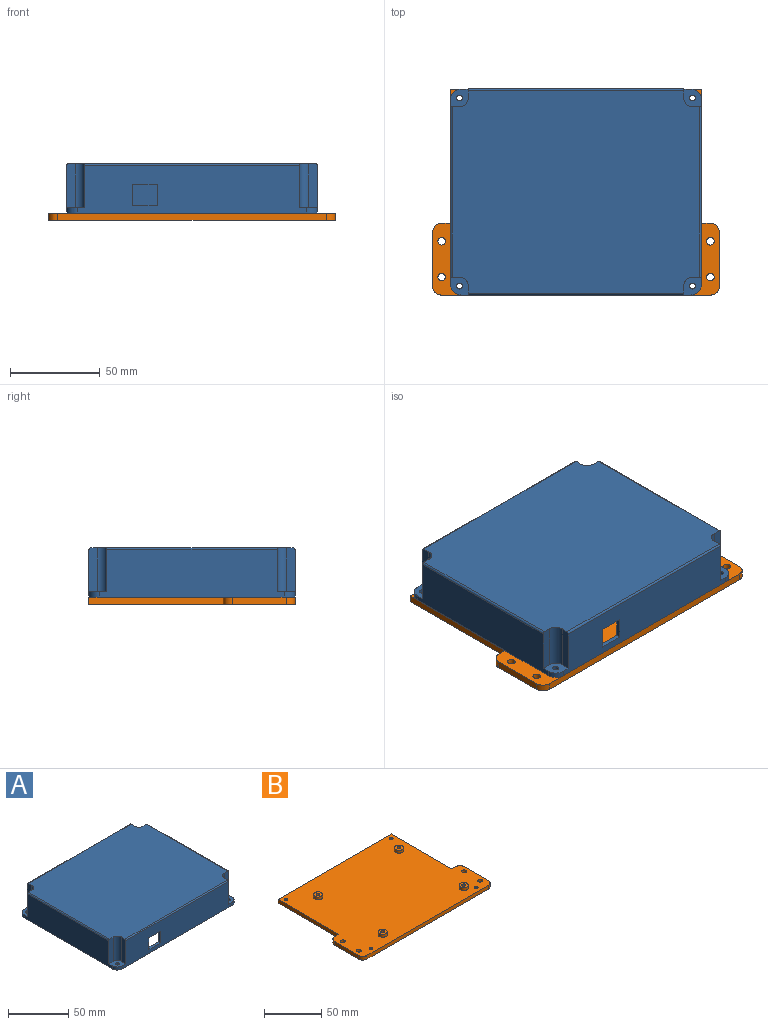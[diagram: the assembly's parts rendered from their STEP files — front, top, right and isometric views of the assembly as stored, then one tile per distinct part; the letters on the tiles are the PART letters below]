
ASSEMBLY  parts=2 mates=1
PART A: 55 faces, bbox 140x115x27.5 mm
  f0: plane 128x26.5mm, normal (0,-1,0), area 3048.3mm2, adj f6,f14,f15,f16,f39,f41,f43,f46
  f1: plane 116x25mm, normal (0,1,0), area 2738mm2, adj f10,f14,f20,f24,f51,f52,f53,f54
  f2: plane 103x26.5mm, normal (-1,0,0), area 2541.5mm2, adj f7,f14,f15,f18,f35,f37,f43,f44
  f3: plane 102.98x26.5mm, normal (1,0,0), area 2541.4mm2, adj f8,f14,f16,f17,f31,f32,f39,f40
  f4: plane 128x26.5mm, normal (0,1,0), area 3210.3mm2, adj f9,f14,f17,f18,f31,f34,f35,f38
  f5: plane 138x113mm, normal (0,0,1), area 15292.3mm2, adj f6,f7,f8,f9,f32,f33,f34,f36
  f6: cylinder r=1mm len=120.27mm, axis (-1,0,0), area 188.9mm2, adj f0,f5,f41,f46
  f7: cylinder r=1mm len=95mm, axis (0,1,0), area 149.2mm2, adj f2,f5,f37,f44
  f8: cylinder r=1mm len=95mm, axis (0,-1,0), area 149.2mm2, adj f3,f5,f32,f40
  f9: cylinder r=1mm len=120.27mm, axis (1,0,0), area 188.9mm2, adj f4,f5,f34,f38
  f10: plane 135x110mm, normal (0,0,-1), area 14519.9mm2, adj f1,f11,f12,f13,f19,f20,f21,f22
  f11: plane 116x25mm, normal (0,-1,0), area 2900mm2, adj f10,f14,f25,f29
  f12: plane 91x25mm, normal (-1,0,0), area 2275mm2, adj f10,f14,f23,f26
  f13: plane 91x25mm, normal (1,0,0), area 2275mm2, adj f10,f14,f19,f28
  f14: plane 140x115mm, normal (0,0,-1), area 1515mm2, adj f0,f1,f2,f3,f4,f11,f12,f13
  f15: cylinder r=6mm len=6mm, axis (0,0,-1), area 28.3mm2, adj f0,f2,f14,f43
  f16: cylinder r=6mm len=6.02mm, axis (0,0,-1), area 28.3mm2, adj f0,f3,f14,f39
  f17: cylinder r=6mm len=6.02mm, axis (0,0,-1), area 28.3mm2, adj f3,f4,f14,f31
  f18: cylinder r=6mm len=6mm, axis (0,0,-1), area 28.3mm2, adj f2,f4,f14,f35
  f19: plane 25x3.5mm, normal (0,1,0), area 87.5mm2, adj f10,f13,f14,f21
  f20: plane 25x3.5mm, normal (1,0,0), area 87.5mm2, adj f1,f10,f14,f21
  f21: cylinder r=6mm len=25mm, axis (0,0,1), area 235.6mm2, adj f10,f14,f19,f20
  f22: cylinder r=6mm len=25mm, axis (0,0,1), area 236.3mm2, adj f10,f14,f23,f24
  f23: plane 25x3.47mm, normal (0,1,0), area 86.8mm2, adj f10,f12,f14,f22
  f24: plane 25x3.5mm, normal (-1,0,0), area 87.5mm2, adj f1,f10,f14,f22
  f25: plane 25x3.5mm, normal (-1,0,0), area 87.5mm2, adj f10,f11,f14,f27
  f26: plane 25x3.47mm, normal (0,-1,0), area 86.8mm2, adj f10,f12,f14,f27
  f27: cylinder r=6mm len=25mm, axis (0,0,1), area 236.3mm2, adj f10,f14,f25,f26
  f28: plane 25x3.5mm, normal (0,-1,0), area 87.5mm2, adj f10,f13,f14,f30
  f29: plane 25x3.5mm, normal (1,0,0), area 87.5mm2, adj f10,f11,f14,f30
  f30: cylinder r=6mm len=25mm, axis (0,0,1), area 235.6mm2, adj f10,f14,f28,f29
  f31: plane 10x10mm, normal (0,0,1), area 78mm2, adj f3,f4,f17,f32,f33,f34,f50
  f32: plane 24.5x5mm, normal (0,1,0), area 122.3mm2, adj f3,f5,f8,f31,f33
  f33: cylinder r=5mm len=24.5mm, axis (0,0,-1), area 195.7mm2, adj f5,f31,f32,f34
  f34: plane 24.51x4.88mm, normal (1,-0.03,0), area 119mm2, adj f4,f5,f9,f31,f33
  f35: plane 10x10mm, normal (0,0,1), area 78mm2, adj f2,f4,f18,f36,f37,f38,f49
  f36: cylinder r=5mm len=24.5mm, axis (0,0,-1), area 195.7mm2, adj f5,f35,f37,f38
  f37: plane 24.5x5mm, normal (0,1,0), area 122.3mm2, adj f2,f5,f7,f35,f36
  f38: plane 24.51x4.88mm, normal (-1,-0.03,0), area 119mm2, adj f4,f5,f9,f35,f36
  f39: plane 10x10mm, normal (0,0,1), area 78mm2, adj f0,f3,f16,f40,f41,f42,f48
  f40: plane 24.5x5mm, normal (0,-1,0), area 122.3mm2, adj f3,f5,f8,f39,f42
  f41: plane 24.51x4.88mm, normal (1,0.03,0), area 119mm2, adj f0,f5,f6,f39,f42
  f42: cylinder r=5mm len=24.5mm, axis (0,0,-1), area 195.7mm2, adj f5,f39,f40,f41
  f43: plane 10x10mm, normal (0,0,1), area 78mm2, adj f0,f2,f15,f44,f45,f46,f47
  f44: plane 24.5x5mm, normal (0,-1,0), area 122.3mm2, adj f2,f5,f7,f43,f45
  f45: cylinder r=5mm len=24.5mm, axis (0,0,-1), area 195.7mm2, adj f5,f43,f44,f46
  f46: plane 24.51x4.88mm, normal (-1,0.03,0), area 119mm2, adj f0,f5,f6,f43,f45
  f47: cylinder r=1.65mm len=3.3mm, axis (0,0,-1), area 31.1mm2, adj f14,f43
  f48: cylinder r=1.65mm len=3.3mm, axis (0,0,-1), area 31.1mm2, adj f14,f39
  f49: cylinder r=1.65mm len=3.3mm, axis (0,0,-1), area 31.1mm2, adj f14,f35
  f50: cylinder r=1.65mm len=3.3mm, axis (0,0,-1), area 31.1mm2, adj f14,f31
  f51: plane 13.5x2.5mm, normal (0,0,-1), area 33.7mm2, adj f0,f1,f52,f54
  f52: plane 12x2.5mm, normal (1,0,0), area 30mm2, adj f0,f1,f51,f53
  f53: plane 13.5x2.5mm, normal (0,0,1), area 33.7mm2, adj f0,f1,f52,f54
  f54: plane 12x2.5mm, normal (-1,0,0), area 30mm2, adj f0,f1,f51,f53
PART B: 90 faces, bbox 160x115x7 mm
  f0: cylinder r=1.7mm len=4.5mm, axis (0,0,-1), area 48.1mm2, adj f9,f89
  f1: cylinder r=1.7mm len=4.5mm, axis (0,0,-1), area 48.1mm2, adj f12,f82
  f2: cylinder r=1.7mm len=4.5mm, axis (0,0,-1), area 48.1mm2, adj f14,f75
  f3: cylinder r=1.7mm len=4.5mm, axis (0,0,-1), area 48.1mm2, adj f16,f68
  f4: cylinder r=1.6mm len=3.2mm, axis (0,0,-1), area 15.1mm2, adj f33,f61
  f5: cylinder r=1.6mm len=3.2mm, axis (0,0,-1), area 15.1mm2, adj f33,f54
  f6: cylinder r=1.6mm len=3.2mm, axis (0,0,-1), area 15.1mm2, adj f33,f47
  f7: cylinder r=1.6mm len=3.2mm, axis (0,0,-1), area 15.1mm2, adj f33,f40
  f8: cylinder r=4mm len=8mm, axis (0,0,-1), area 75.4mm2, adj f9,f33
  f9: plane 8x8mm, normal (0,0,1), area 41.2mm2, adj f0,f8
  f10: plane 160x115mm, normal (0,0,-1), area 16613.5mm2, adj f17,f18,f19,f20,f21,f22,f23,f24
  f11: cylinder r=4mm len=8mm, axis (0,0,-1), area 75.4mm2, adj f12,f33
  f12: plane 8x8mm, normal (0,0,1), area 41.2mm2, adj f1,f11
  f13: cylinder r=4mm len=8mm, axis (0,0,-1), area 75.4mm2, adj f14,f33
  f14: plane 8x8mm, normal (0,0,1), area 41.2mm2, adj f2,f13
  f15: cylinder r=4mm len=8mm, axis (0,0,-1), area 75.4mm2, adj f16,f33
  f16: plane 8x8mm, normal (0,0,1), area 41.2mm2, adj f3,f15
  f17: plane 75x4mm, normal (-1,0,0), area 300mm2, adj f10,f18,f32,f33
  f18: plane 5x4mm, normal (0,1,0), area 20mm2, adj f10,f17,f19,f33
  f19: cylinder r=5mm len=5mm, axis (0,0,-1), area 31.4mm2, adj f10,f18,f20,f33
  f20: plane 30x4mm, normal (-1,0,0), area 120mm2, adj f10,f19,f21,f33
  f21: cylinder r=5mm len=5mm, axis (0,0,-1), area 31.4mm2, adj f10,f20,f22,f33
  f22: plane 150x4mm, normal (0,-1,0), area 600mm2, adj f10,f21,f23,f33
  f23: cylinder r=5mm len=5mm, axis (0,0,-1), area 31.4mm2, adj f10,f22,f24,f33
  f24: plane 30x4mm, normal (1,0,0), area 120mm2, adj f10,f23,f25,f33
  f25: cylinder r=5mm len=5mm, axis (0,0,-1), area 31.4mm2, adj f10,f24,f26,f33
  f26: plane 5x4mm, normal (0,1,0), area 20mm2, adj f10,f25,f27,f33
  f27: plane 75x4mm, normal (1,0,0), area 300mm2, adj f10,f26,f32,f33
  f28: cylinder r=2.1mm len=4.2mm, axis (0,0,-1), area 52.8mm2, adj f10,f33
  f29: cylinder r=2.1mm len=4.2mm, axis (0,0,-1), area 52.8mm2, adj f10,f33
  f30: cylinder r=2.1mm len=4.2mm, axis (0,0,-1), area 52.8mm2, adj f10,f33
  f31: cylinder r=2.1mm len=4.2mm, axis (0,0,-1), area 52.8mm2, adj f10,f33
  f32: plane 140x4mm, normal (0,1,0), area 560mm2, adj f10,f17,f27,f33
  f33: plane 160x115mm, normal (0,0,1), area 16589.9mm2, adj f4,f5,f6,f7,f8,f11,f13,f15
  f34: plane 3.18x2.5mm, normal (0,1,0), area 7.9mm2, adj f10,f35,f39,f40
  f35: plane 2.75x2.5mm, normal (0.87,0.5,0), area 7.9mm2, adj f10,f34,f36,f40
  f36: plane 2.75x2.5mm, normal (0.87,-0.5,0), area 7.9mm2, adj f10,f35,f37,f40
  f37: plane 3.18x2.5mm, normal (0,-1,0), area 7.9mm2, adj f10,f36,f38,f40
  f38: plane 2.75x2.5mm, normal (-0.87,-0.5,0), area 7.9mm2, adj f10,f37,f39,f40
  f39: plane 2.75x2.5mm, normal (-0.87,0.5,0), area 7.9mm2, adj f10,f34,f38,f40
  f40: plane 6.35x5.5mm, normal (0,0,-1), area 18.2mm2, adj f7,f34,f35,f36,f37,f38,f39
  f41: plane 3.18x2.5mm, normal (0,1,0), area 7.9mm2, adj f10,f42,f46,f47
  f42: plane 2.75x2.5mm, normal (0.87,0.5,0), area 7.9mm2, adj f10,f41,f43,f47
  f43: plane 2.75x2.5mm, normal (0.87,-0.5,0), area 7.9mm2, adj f10,f42,f44,f47
  f44: plane 3.18x2.5mm, normal (0,-1,0), area 7.9mm2, adj f10,f43,f45,f47
  f45: plane 2.75x2.5mm, normal (-0.87,-0.5,0), area 7.9mm2, adj f10,f44,f46,f47
  f46: plane 2.75x2.5mm, normal (-0.87,0.5,0), area 7.9mm2, adj f10,f41,f45,f47
  f47: plane 6.35x5.5mm, normal (0,0,-1), area 18.2mm2, adj f6,f41,f42,f43,f44,f45,f46
  f48: plane 2.75x2.5mm, normal (-0.87,0.5,0), area 7.9mm2, adj f10,f49,f53,f54
  f49: plane 3.18x2.5mm, normal (0,1,0), area 7.9mm2, adj f10,f48,f50,f54
  f50: plane 2.75x2.5mm, normal (0.87,0.5,0), area 7.9mm2, adj f10,f49,f51,f54
  f51: plane 2.75x2.5mm, normal (0.87,-0.5,0), area 7.9mm2, adj f10,f50,f52,f54
  f52: plane 3.18x2.5mm, normal (0,-1,0), area 7.9mm2, adj f10,f51,f53,f54
  f53: plane 2.75x2.5mm, normal (-0.87,-0.5,0), area 7.9mm2, adj f10,f48,f52,f54
  f54: plane 6.35x5.5mm, normal (0,0,-1), area 18.2mm2, adj f5,f48,f49,f50,f51,f52,f53
  f55: plane 3.18x2.5mm, normal (0,1,0), area 7.9mm2, adj f10,f56,f60,f61
  f56: plane 2.75x2.5mm, normal (0.87,0.5,0), area 7.9mm2, adj f10,f55,f57,f61
  f57: plane 2.75x2.5mm, normal (0.87,-0.5,0), area 7.9mm2, adj f10,f56,f58,f61
  f58: plane 3.18x2.5mm, normal (0,-1,0), area 7.9mm2, adj f10,f57,f59,f61
  f59: plane 2.75x2.5mm, normal (-0.87,-0.5,0), area 7.9mm2, adj f10,f58,f60,f61
  f60: plane 2.75x2.5mm, normal (-0.87,0.5,0), area 7.9mm2, adj f10,f55,f59,f61
  f61: plane 6.35x5.5mm, normal (0,0,-1), area 18.2mm2, adj f4,f55,f56,f57,f58,f59,f60
  f62: plane 3.18x2.5mm, normal (0,1,0), area 7.9mm2, adj f10,f63,f67,f68
  f63: plane 2.75x2.5mm, normal (0.87,0.5,0), area 7.9mm2, adj f10,f62,f64,f68
  f64: plane 2.75x2.5mm, normal (0.87,-0.5,0), area 7.9mm2, adj f10,f63,f65,f68
  f65: plane 3.18x2.5mm, normal (0,-1,0), area 7.9mm2, adj f10,f64,f66,f68
  f66: plane 2.75x2.5mm, normal (-0.87,-0.5,0), area 7.9mm2, adj f10,f65,f67,f68
  f67: plane 2.75x2.5mm, normal (-0.87,0.5,0), area 7.9mm2, adj f10,f62,f66,f68
  f68: plane 6.35x5.5mm, normal (0,0,-1), area 17.1mm2, adj f3,f62,f63,f64,f65,f66,f67
  f69: plane 2.75x2.5mm, normal (0.87,-0.5,0), area 7.9mm2, adj f10,f70,f74,f75
  f70: plane 3.18x2.5mm, normal (0,-1,0), area 7.9mm2, adj f10,f69,f71,f75
  f71: plane 2.75x2.5mm, normal (-0.87,-0.5,0), area 7.9mm2, adj f10,f70,f72,f75
  f72: plane 2.75x2.5mm, normal (-0.87,0.5,0), area 7.9mm2, adj f10,f71,f73,f75
  f73: plane 3.18x2.5mm, normal (0,1,0), area 7.9mm2, adj f10,f72,f74,f75
  f74: plane 2.75x2.5mm, normal (0.87,0.5,0), area 7.9mm2, adj f10,f69,f73,f75
  f75: plane 6.35x5.5mm, normal (0,0,-1), area 17.1mm2, adj f2,f69,f70,f71,f72,f73,f74
  f76: plane 3.18x2.5mm, normal (0,1,0), area 7.9mm2, adj f10,f77,f81,f82
  f77: plane 2.75x2.5mm, normal (0.87,0.5,0), area 7.9mm2, adj f10,f76,f78,f82
  f78: plane 2.75x2.5mm, normal (0.87,-0.5,0), area 7.9mm2, adj f10,f77,f79,f82
  f79: plane 3.18x2.5mm, normal (0,-1,0), area 7.9mm2, adj f10,f78,f80,f82
  f80: plane 2.75x2.5mm, normal (-0.87,-0.5,0), area 7.9mm2, adj f10,f79,f81,f82
  f81: plane 2.75x2.5mm, normal (-0.87,0.5,0), area 7.9mm2, adj f10,f76,f80,f82
  f82: plane 6.35x5.5mm, normal (0,0,-1), area 17.1mm2, adj f1,f76,f77,f78,f79,f80,f81
  f83: plane 3.18x2.5mm, normal (0,1,0), area 7.9mm2, adj f10,f84,f88,f89
  f84: plane 2.75x2.5mm, normal (0.87,0.5,0), area 7.9mm2, adj f10,f83,f85,f89
  f85: plane 2.75x2.5mm, normal (0.87,-0.5,0), area 7.9mm2, adj f10,f84,f86,f89
  f86: plane 3.18x2.5mm, normal (0,-1,0), area 7.9mm2, adj f10,f85,f87,f89
  f87: plane 2.75x2.5mm, normal (-0.87,-0.5,0), area 7.9mm2, adj f10,f86,f88,f89
  f88: plane 2.75x2.5mm, normal (-0.87,0.5,0), area 7.9mm2, adj f10,f83,f87,f89
  f89: plane 6.35x5.5mm, normal (0,0,-1), area 17.1mm2, adj f0,f83,f84,f85,f86,f87,f88
PLACE A t=(0,0,4)mm
PLACE B at identity fixed
MATE fastened A.f45 <-> B.f5  axis (0,0,-1) through (5,5,4)mm
